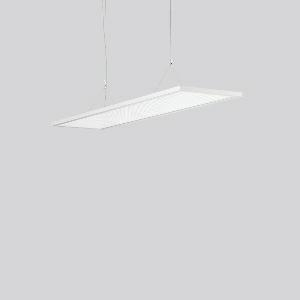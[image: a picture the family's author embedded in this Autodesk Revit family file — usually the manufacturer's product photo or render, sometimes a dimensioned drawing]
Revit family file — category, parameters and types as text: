
# Revit family: sidelite_square_312271_004_76_8ecb
name_source: partatom
category: Lighting Fixtures
units: mm (PartAtom-declared; Revit-internal decimal feet)

## family parameters
Cut with Voids When Loaded = No
Host = Face
Light Source = No
Part Type = Normal
Room Calculation Point = No
Round Connector Dimension = Use Diameter
Shared = No

## types (1)
- SIDELITE square (1 x LED Modul 830, 3950 lm, 3000)
    Apparent Load = 33 VA
    CIE Flux Codes = 63 89 97 100 100
    Color Rendering = 80
    Color Temperature = 3000
    Default Elevation = 1800 mm
    Description = Series: SIDELITE
Aesthetically pleasing pendant-mounted surface luminaire with extremely flat profile and progressive LED technology. Cover made of sheet steel, powder-coated. Frame: extruded anodised aluminium profile. Diffuser with microstructure. Lightguide and diffuser made of non-yellowing plastic (PMMA). Lateral light emission (RZB SIDELITE technology) for above-average homogeneous light distribution. Very easy installation thanks to Plug+Play connection. 2-point steel cable suspension, steplessly adjustable. Special lengths available on request. Driver integrated. Perfect for office areas (RUG < 19) and environments with computer screens in accordance with EN 12464-1. 
Colour: anodised aluminium
Length: 1198 mm
Width: 298 mm
Height: 49 mm
Suspension length: 300-3000 mm
Lamp: LED
Socket: without socket
Colour temperature: 3000K
Colour rendering index (CRI): 80
System power: 33 W
Rated luminous flux: 3950 lm
Beam angle Down: 92° / 91°
Luminous efficiency: 120 lm/W
Control gear: Converter, dimmable, DALI
Protection class: I
Type of protection: IP 40
    Height = 49 mm
    Lamp = 1 x LED Modul 830
    Lamp Light Flux = 3950 lm
    Lamp count = 1
    Length = 1198 mm
    Lifetime = 50000 h
    Luminous efficacy = 120 lm/W
    Manufacturer = RZB
    ModVariant = No
    Model = 312271.004.76
    Mounting Place = Ceiling
    Mounting Type = Pendant
    Number of Poles = 1
    OnlyDefault = Yes
    Power Factor = 1
    Product Name = SIDELITE square
    Product group = Pendant modular luminaires
    ProductGroupID = 906
    Protection Class = Protection class I
    Protection Degree = IP 40
    RLX_Detail_Level = 1
    RLX_Emergency_Light_Flux = 0 lm
    RLX_Emergency_Type = 0
    RLX_Emergency_Type_DB = No
    RlxData = <blob elided: 20713 chars, md5=3d8aa0a8>
    Socket = socket
    Standby Power = 0 W
    System Light Flux = 3950 lm
    System Power = 33 W
    Type Comments = ALEA SPOT
    Type Image = 312271.000.jpg
    URL = http://relux.com
    VarID = ---
    Voltage = 230 V
    Voltage Range = 220-240 V
    Weight = 0.00 kg
    Width = 298 mm

## geometry (parser evidence)
native form markers: Blend x4, Sweep x12
no freeform markers — native parametric forms only
